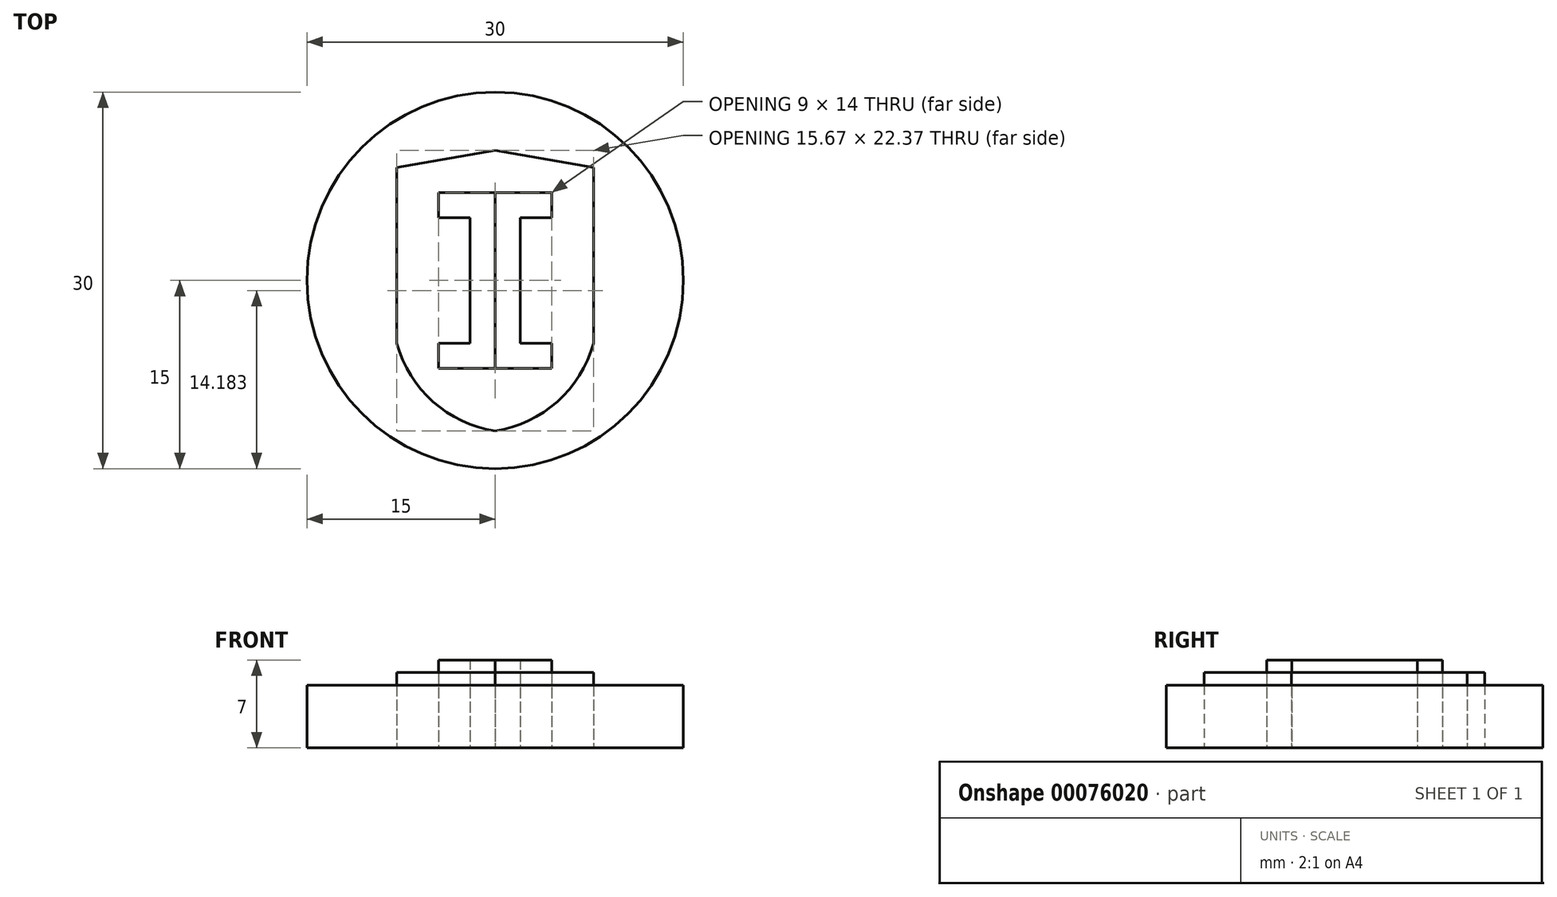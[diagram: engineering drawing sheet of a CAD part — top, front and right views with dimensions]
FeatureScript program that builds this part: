
annotation { "Feature Type Name" : "Feature", "Feature Type Description" : "" }
export const myFeature = defineFeature(function(context is Context, id is Id, definition is map)
    precondition{}
    {
        {
            var Q0;
            Q0=qCreatedBy(makeId("Top.planeOp"),FACE);
            var sketch = newSketch(context, id + "F0", { "sketchPlane" : qUnion([Q0])});
            skCircle(sketch, "E0", {"center": v(0, 0) * mm, "radius": 15 * mm});
            skLineSegment(sketch, "E1", {"start": v(-4.5, 7) * mm, "end": v(-4.5, 5) * mm});
            skLineSegment(sketch, "E2", {"start": v(-4.5, 5) * mm, "end": v(-2, 5) * mm});
            skLineSegment(sketch, "E3", {"start": v(-2, 5) * mm, "end": v(-2, -5) * mm});
            skLineSegment(sketch, "E4", {"start": v(-2, -5) * mm, "end": v(-4.5, -5) * mm});
            skLineSegment(sketch, "E5", {"start": v(-4.5, -5) * mm, "end": v(-4.5, -7) * mm});
            skLineSegment(sketch, "E6", {"start": v(-4.5, -7) * mm, "end": v(4.5, -7) * mm});
            skLineSegment(sketch, "E7", {"start": v(4.5, -7) * mm, "end": v(4.5, -5) * mm});
            skLineSegment(sketch, "E8", {"start": v(4.5, -5) * mm, "end": v(2, -5) * mm});
            skLineSegment(sketch, "E9", {"start": v(2, -5) * mm, "end": v(2, 5) * mm});
            skLineSegment(sketch, "E10", {"start": v(2, 5) * mm, "end": v(4.5, 5) * mm});
            skLineSegment(sketch, "E11", {"start": v(4.5, 5) * mm, "end": v(4.5, 7) * mm});
            skLineSegment(sketch, "E12", {"start": v(4.5, 7) * mm, "end": v(-4.5, 7) * mm});
            skLineSegment(sketch, "E13", {"start": v(0, 10.37) * mm, "end": v(7.84, 8.98) * mm});
            skLineSegment(sketch, "E14", {"start": v(7.84, 8.98) * mm, "end": v(7.84, -5.02) * mm});
            skLineSegment(sketch, "E15", {"start": v(0, 10.37) * mm, "end": v(-7.84, 8.98) * mm});
            skLineSegment(sketch, "E16", {"start": v(-7.84, 8.98) * mm, "end": v(-7.84, -5.02) * mm});
            skArc(sketch, "E17", {"start": v(-7.84, -5.02) * mm, "mid": v(-4.95, -9.67) * mm, "end": v(0, -12) * mm});
            skArc(sketch, "E18", {"start": v(0, -12) * mm, "mid": v(4.95, -9.67) * mm, "end": v(7.84, -5.02) * mm});
            skLineSegment(sketch, "E19", {"start": v(0, 7) * mm, "end": v(0, -7) * mm});
            skSolve(sketch);
        }
        {
            var Q0;
            Q0=makeQuery(id+"F0.imprint","IMPRINT",FACE,{"disambiguationData":[TD([[makeQuery(id+"F0.imprint","IMPRINT",EDGE,{"derivedFrom":sQuery(id+"F0.wireOp",EDGE,"E0")}),1.0]])]});
            extrude(context, id + "F1", {"entities" : qUnion([Q0]), "depth" : 5 * mm});
        }
        {
            var Q0;
            Q0=makeQuery(id+"F0.imprint","IMPRINT",FACE,{"disambiguationData":[TD([[makeQuery(id+"F0.imprint","IMPRINT",EDGE,{"derivedFrom":sQuery(id+"F0.wireOp",EDGE,"E1")}),-1.0]])]});
            extrude(context, id + "F2", {"entities" : qUnion([Q0]), "depth" : 6 * mm});
        }
        {
            var Q0;
            Q0=makeQuery(id+"F0.imprint","IMPRINT",FACE,{"disambiguationData":[TD([[makeQuery(id+"F0.imprint","IMPRINT",EDGE,{"derivedFrom":sQuery(id+"F0.wireOp",EDGE,"E1")}),1.0]])]});
            extrude(context, id + "F3", {"entities" : qUnion([Q0]), "depth" : 7 * mm});
        }
        {
            var Q0;
            {var subQ0=sQuery(id+"F0.wireOp",EDGE,"E7");Q0=makeQuery(id+"F0.imprint","IMPRINT",FACE,{"disambiguationData":[TD([[makeQuery(id+"F0.imprint","IMPRINT",EDGE,{"derivedFrom":subQ0}),1.0]])]});}
            extrude(context, id + "F4", {"entities" : qUnion([Q0]), "depth" : 7 * mm});
        }
    });
